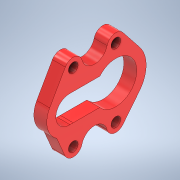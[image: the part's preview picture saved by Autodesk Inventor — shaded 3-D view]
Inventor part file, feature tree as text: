
AUTODESK INVENTOR PART (.ipt)
format: ipt  version: 2021 (Build 250183000, 183)  size: 158,208 bytes
history: native  units: in
note: dims shown in document units (in); Inventor stores cm internally (conversion verified against a paired STEP export)
features: extrude x1, sketch x1
ambient origin geometry x8: Origin, YZ Plane, XZ Plane, XY Plane, X Axis, Y Axis, Z Axis, Center Point
bodies: Solid1 (feature_tree)
feature tree (2):
  extrude  "Extrusion1"  Depth=0.7874in
  sketch  "Sketch1"  dims[d15=0.5906in d16=0.7874in d17=1.2795in d18=1.8504in d19=0.8268in d20=2.8346in d21=4.1732in d22=2.5984in d23=0.5906in d24=0.7874in d25=0.0in]
